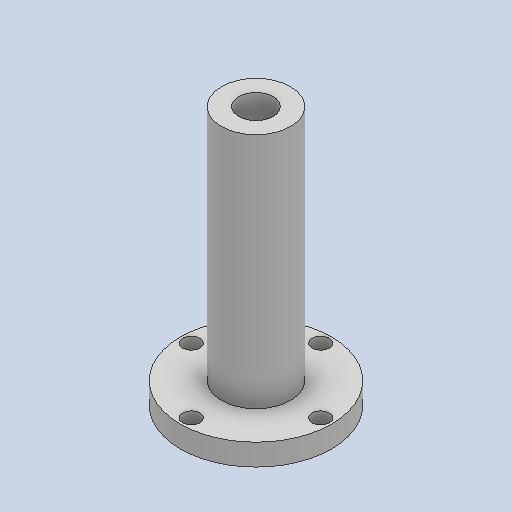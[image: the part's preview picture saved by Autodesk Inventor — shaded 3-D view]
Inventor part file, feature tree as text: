
AUTODESK INVENTOR PART (.ipt)
format: ipt  version: 2023 (Build 270158000, 158)  size: 142,848 bytes
history: native  units: mm
features: extrude x3, sketch x3
ambient origin geometry x8: Origin, YZ Plane, XZ Plane, XY Plane, X Axis, Y Axis, Z Axis, Center Point
bodies: Solid1 (feature_tree)
feature tree (6):
  extrude  "Extrusion1"  Depth=8.0mm
  extrude  "Extrusion2"  Depth=5.0mm
  extrude  "Extrusion3"  Depth=55.0mm
  sketch  "Sketch3"  dims[d0=8.0mm d1=35.0mm]
  sketch  "Sketch4"  dims[d2=5.0mm d3=0.0mm d4=16.0mm]
  sketch  "Sketch5"  dims[d5=8.0mm d6=55.0mm d7=0.0mm d8=4.0mm d9=15.0mm d10=15.0mm d11=15.0mm d12=15.0mm d13=4.0mm d14=4.0mm d15=4.0mm d16=55.0mm d17=0.0mm]
